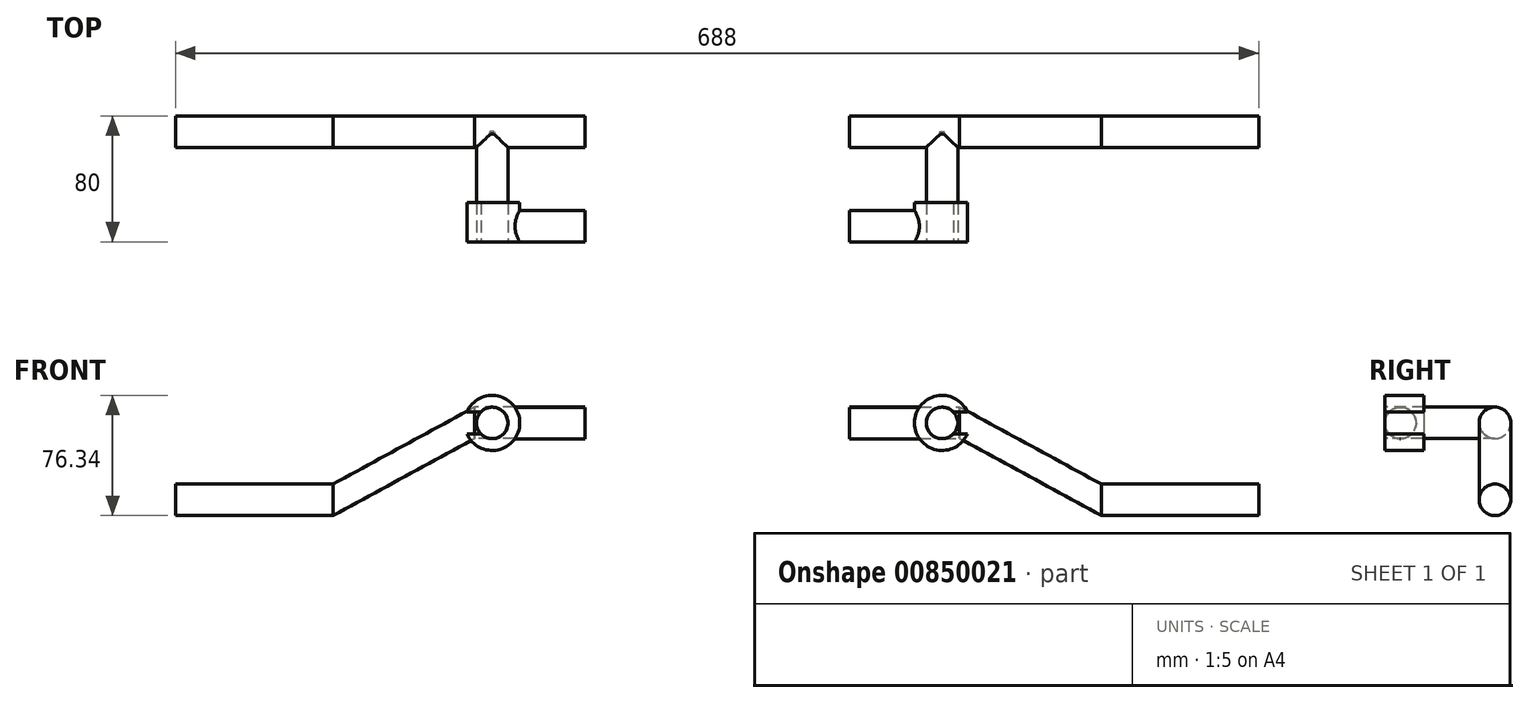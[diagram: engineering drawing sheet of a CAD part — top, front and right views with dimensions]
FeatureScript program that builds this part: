
annotation { "Feature Type Name" : "Feature", "Feature Type Description" : "" }
export const myFeature = defineFeature(function(context is Context, id is Id, definition is map)
    precondition{}
    {
        {
            var Q0;
            Q0=qCreatedBy(makeId("Right.planeOp"),FACE);
            var sketch = newSketch(context, id + "F0", { "sketchPlane" : qUnion([Q0])});
            skCircle(sketch, "E0", {"center": v(0, 0) * mm, "radius": 10 * mm});
            skSolve(sketch);
        }
        {
            var Q0;
            Q0 = qSketchRegion(id + "F0", true);
            extrude(context, id + "F1", {"entities" : qUnion([Q0]), "depth" : 100 * mm, "offsetDistance" : 25 * mm});
        }
        {
            var Q0;
            Q0=qCreatedBy(makeId("Right.planeOp"),FACE);
            cPlane(context, id + "F2", {"entities" : qUnion([Q0]), "cplaneType" : CPlaneType.OFFSET, "offset" : 30 * mm, "oppositeDirection" : true, "width" : 150 * mm, "height" : 150 * mm});
        }
        {
            var Q0;
            Q0=qCreatedBy(id+"F2.planeOp",FACE);
            cPlane(context, id + "F3", {"entities" : qUnion([Q0]), "cplaneType" : CPlaneType.OFFSET, "offset" : 60 * mm, "oppositeDirection" : true, "width" : 150 * mm, "height" : 150 * mm});
        }
        {
            var Q0;
            Q0=qCreatedBy(id+"F3.planeOp",FACE);
            var sketch = newSketch(context, id + "F4", { "sketchPlane" : qUnion([Q0])});
            skCircle(sketch, "E1", {"center": v(0, 48.93) * mm, "radius": 10 * mm});
            skSolve(sketch);
        }
        {
            var Q0;
            Q0=makeQuery(id+"F1.opExtrude","CAP_FACE",FACE,{"disambiguationData":[OSD([sQuery(id+"F0.wireOp",EDGE,"E0")])],"isStart":true});
            var Q1;
            Q1=makeQuery(id+"F4.imprint","IMPRINT",FACE,{"disambiguationData":[TD([[makeQuery(id+"F4.imprint","IMPRINT",EDGE,{"derivedFrom":sQuery(id+"F4.wireOp",EDGE,"E1")}),1.0]])]});
            loft(context, id + "F5", {"sheetProfilesArray" : [{ "sheetProfileEntities" : qUnion([Q0]) }, { "sheetProfileEntities" : qUnion([Q1]) }]});
        }
        {
            var Q0;
            Q0=makeQuery(id+"F5.opLoft","CAP_FACE",FACE,{"disambiguationData":[OSD([makeQuery(id+"F4.imprint","IMPRINT",FACE,{"disambiguationData":[TD([[makeQuery(id+"F4.imprint","IMPRINT",EDGE,{"derivedFrom":sQuery(id+"F4.wireOp",EDGE,"E1")}),1.0]])]})])],"isStart":true});
            extrude(context, id + "F6", {"entities" : qUnion([Q0]), "operationType" : NewBodyOperationType.ADD, "depth" : 70 * mm, "offsetDistance" : 25 * mm});
        }
        {
            var Q0;
            Q0=qCreatedBy(makeId("Front.planeOp"),FACE);
            cPlane(context, id + "F7", {"entities" : qUnion([Q0]), "cplaneType" : CPlaneType.OFFSET, "offset" : 70 * mm, "width" : 150 * mm, "height" : 150 * mm});
        }
        {
            var Q0;
            Q0=qCreatedBy(id+"F7.planeOp",FACE);
            var sketch = newSketch(context, id + "F8", { "sketchPlane" : qUnion([Q0])});
            skCircle(sketch, "E2", {"center": v(-101.3, 48.81) * mm, "radius": 10 * mm});
            skSolve(sketch);
        }
        {
            var Q0;
            Q0=makeQuery(id+"F8.imprint","IMPRINT",FACE,{"disambiguationData":[TD([[makeQuery(id+"F8.imprint","IMPRINT",EDGE,{"derivedFrom":sQuery(id+"F8.wireOp",EDGE,"E2")}),1.0]])]});
            extrude(context, id + "F9", {"entities" : qUnion([Q0]), "operationType" : NewBodyOperationType.ADD, "oppositeDirection" : true, "depth" : 30 * mm, "offsetDistance" : 25 * mm});
        }
        {
            var Q0;
            Q0=makeQuery(id+"F9.opExtrude","SWEPT_BODY",BODY,{"disambiguationData":[OSD([sQuery(id+"F8.wireOp",EDGE,"E2")])]});
            deleteBodies(context, id + "F10", {"entities" : qUnion([Q0])});
        }
        {
            var Q0;
            Q0=qCreatedBy(id+"F7.planeOp",FACE);
            var sketch = newSketch(context, id + "F11", { "sketchPlane" : qUnion([Q0])});
            skCircle(sketch, "E3", {"center": v(-101.14, 48.84) * mm, "radius": 10 * mm});
            skSolve(sketch);
        }
        {
            var Q0;
            Q0=makeQuery(id+"F11.imprint","IMPRINT",FACE,{"disambiguationData":[TD([[makeQuery(id+"F11.imprint","IMPRINT",EDGE,{"derivedFrom":sQuery(id+"F11.wireOp",EDGE,"E3")}),1.0]])]});
            extrude(context, id + "F12", {"entities" : qUnion([Q0]), "operationType" : NewBodyOperationType.ADD, "oppositeDirection" : true, "depth" : 70 * mm, "offsetDistance" : 25 * mm});
        }
        {
            var Q0;
            Q0=makeQuery(id+"F12.opExtrude","CAP_FACE",FACE,{"disambiguationData":[OSD([sQuery(id+"F11.wireOp",EDGE,"E3")])],"isStart":true});
            var sketch = newSketch(context, id + "F13", { "sketchPlane" : qUnion([Q0])});
            skArc(sketch, "E4", {"start": v(-85.1, 55.84) * mm, "mid": v(-118.64, 48.84) * mm, "end": v(-85.1, 41.84) * mm});
            skLineSegment(sketch, "E5", {"start": v(-94, 55.84) * mm, "end": v(-85.1, 55.84) * mm});
            skLineSegment(sketch, "E6", {"start": v(-94, 41.84) * mm, "end": v(-85.1, 41.84) * mm});
            skCircle(sketch, "E7", {"center": v(-101.14, 48.84) * mm, "radius": 10 * mm});
            skPoint(sketch, "E8.orphan", {"position": v(-101.14, 55.84) * mm});
            skPoint(sketch, "E9.orphan", {"position": v(-101.14, 41.84) * mm});
            skSolve(sketch);
        }
        {
            var Q0;
            Q0=makeQuery(id+"F13.imprint","IMPRINT",FACE,{"disambiguationData":[TD([[makeQuery(id+"F13.imprint","IMPRINT",EDGE,{"derivedFrom":sQuery(id+"F13.wireOp",EDGE,"E4")}),1.0]])]});
            extrude(context, id + "F14", {"entities" : qUnion([Q0]), "oppositeDirection" : true, "depth" : 25 * mm, "offsetDistance" : 25 * mm});
        }
        {
            var Q0;
            Q0=makeQuery(id+"F6.opExtrude","CAP_FACE",FACE,{"disambiguationData":[OSD([makeQuery(id+"F4.imprint","IMPRINT",FACE,{"disambiguationData":[TD([[makeQuery(id+"F4.imprint","IMPRINT",EDGE,{"derivedFrom":sQuery(id+"F4.wireOp",EDGE,"E1")}),1.0]])]})])],"isStart":false});
            var sketch = newSketch(context, id + "F15", { "sketchPlane" : qUnion([Q0])});
            skCircle(sketch, "E10", {"center": v(60, 48.79) * mm, "radius": 10 * mm});
            skCircle(sketch, "E11", {"center": v(0, 48.79) * mm, "radius": 10 * mm});
            skSolve(sketch);
        }
        {
            var Q0;
            Q0=makeQuery(id+"F15.imprint","IMPRINT",FACE,{"disambiguationData":[TD([[makeQuery(id+"F15.imprint","IMPRINT",EDGE,{"derivedFrom":sQuery(id+"F15.wireOp",EDGE,"E10")}),1.0]])]});
            extrude(context, id + "F16", {"entities" : qUnion([Q0]), "operationType" : NewBodyOperationType.ADD, "oppositeDirection" : true, "depth" : 48 * mm, "offsetDistance" : 25 * mm});
        }
        {
            var Q0;
            Q0=qCreatedBy(id+"F3.planeOp",FACE);
            cPlane(context, id + "F17", {"entities" : qUnion([Q0]), "cplaneType" : CPlaneType.OFFSET, "offset" : 154 * mm, "oppositeDirection" : true, "width" : 150 * mm, "height" : 150 * mm});
        }
        {
            var Q0;
            Q0=makeQuery(id+"F5.opLoft","SWEPT_BODY",BODY,{"disambiguationData":[OSD([sQuery(id+"F0.wireOp",EDGE,"E0"),makeQuery(id+"F4.imprint","IMPRINT",FACE,{"disambiguationData":[TD([[makeQuery(id+"F4.imprint","IMPRINT",EDGE,{"derivedFrom":sQuery(id+"F4.wireOp",EDGE,"E1")}),1.0]])]})])]});
            var Q1;
            Q1=makeQuery(id+"F1.opExtrude","SWEPT_BODY",BODY,{"disambiguationData":[OSD([sQuery(id+"F0.wireOp",EDGE,"E0")])]});
            var Q2;
            Q2=makeQuery(id+"F14.opExtrude","SWEPT_BODY",BODY,{"disambiguationData":[OSD([sQuery(id+"F13.wireOp",EDGE,"E4"),sQuery(id+"F13.wireOp",EDGE,"E5"),sQuery(id+"F13.wireOp",EDGE,"E6"),sQuery(id+"F13.wireOp",EDGE,"E7")])]});
            var Q3;
            Q3=qCreatedBy(id+"F17.planeOp",FACE);
            mirror(context, id + "F18", {"entities" : qUnion([Q0, Q1, Q2]), "mirrorPlane" : qUnion([Q3])});
        }
    });
